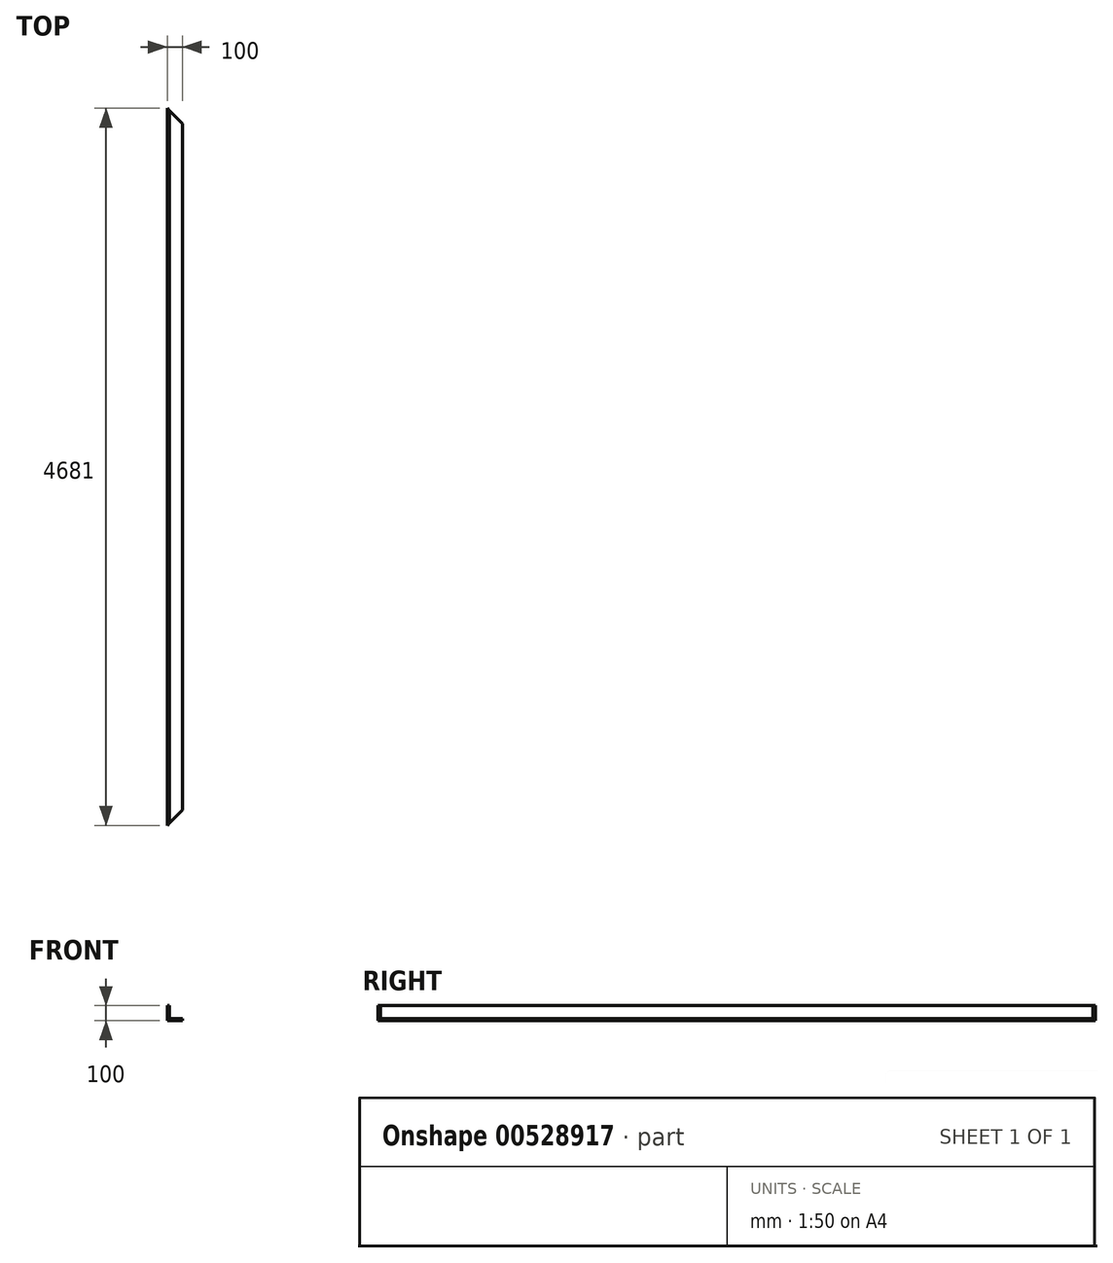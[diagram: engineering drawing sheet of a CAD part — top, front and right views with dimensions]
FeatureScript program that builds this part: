
annotation { "Feature Type Name" : "Feature", "Feature Type Description" : "" }
export const myFeature = defineFeature(function(context is Context, id is Id, definition is map)
    precondition{}
    {
        {
            var Q0;
            Q0=qCreatedBy(makeId("Top.planeOp"),FACE);
            var sketch = newSketch(context, id + "F0", { "sketchPlane" : qUnion([Q0])});
            skLineSegment(sketch, "E0", {"start": v(0, -2340.5) * mm, "end": v(0, 2340.5) * mm});
            skLineSegment(sketch, "E1", {"start": v(-100, -2240.5) * mm, "end": v(-100, 2240.5) * mm});
            skLineSegment(sketch, "E2", {"start": v(0, -2340.5) * mm, "end": v(-100, -2240.5) * mm});
            skLineSegment(sketch, "E3", {"start": v(0, 2340.5) * mm, "end": v(-100, 2240.5) * mm});
            skSolve(sketch);
        }
        {
            var Q0;
            Q0=makeQuery(id+"F0.imprint","IMPRINT",FACE,{"disambiguationData":[TD([[makeQuery(id+"F0.imprint","IMPRINT",EDGE,{"derivedFrom":sQuery(id+"F0.wireOp",EDGE,"E0")}),1.0]])]});
            extrude(context, id + "F1", {"entities" : qUnion([Q0]), "depth" : 15 * mm, "offsetDistance" : 25 * mm});
        }
        {
            var Q0;
            Q0=makeQuery(id+"F1.opExtrude","CAP_FACE",FACE,{"disambiguationData":[OSD([sQuery(id+"F0.wireOp",EDGE,"E0"),sQuery(id+"F0.wireOp",EDGE,"E1"),sQuery(id+"F0.wireOp",EDGE,"E2"),sQuery(id+"F0.wireOp",EDGE,"E3")])],"isStart":false});
            var sketch = newSketch(context, id + "F2", { "sketchPlane" : qUnion([Q0])});
            skLineSegment(sketch, "E4.0", {"start": v(0, -2340.5) * mm, "end": v(0, 2340.5) * mm});
            skLineSegment(sketch, "E5", {"start": v(-15, 2325.5) * mm, "end": v(-15, -2325.5) * mm});
            skLineSegment(sketch, "E6", {"start": v(0, 2340.5) * mm, "end": v(-15, 2325.5) * mm});
            skLineSegment(sketch, "E7", {"start": v(-15, -2325.5) * mm, "end": v(0, -2340.5) * mm});
            skSolve(sketch);
        }
        {
            var Q0;
            Q0=makeQuery(id+"F2.imprint","IMPRINT",FACE,{"disambiguationData":[TD([[makeQuery(id+"F2.imprint","IMPRINT",EDGE,{"derivedFrom":sQuery(id+"F2.wireOp",EDGE,"E4.0")}),1.0]])]});
            extrude(context, id + "F3", {"entities" : qUnion([Q0]), "operationType" : NewBodyOperationType.ADD, "depth" : (100 - 15) * mm, "offsetDistance" : 25 * mm});
        }
        {
            var Q0;
            Q0=makeQuery(id+"F1.opExtrude","SWEPT_BODY",BODY,{"disambiguationData":[OSD([sQuery(id+"F0.wireOp",EDGE,"E0"),sQuery(id+"F0.wireOp",EDGE,"E1"),sQuery(id+"F0.wireOp",EDGE,"E2"),sQuery(id+"F0.wireOp",EDGE,"E3")])]});
            var Q1;
            Q1=makeQuery(id+"F3.boolean.opBoolean","MERGE",FACE,{"derivedFrom":[makeQuery(id+"F1.opExtrude","SWEPT_FACE",FACE,{"disambiguationData":[OSD([sQuery(id+"F0.wireOp",EDGE,"E0")])]}),makeQuery(id+"F3.opExtrude","SWEPT_FACE",FACE,{"disambiguationData":[OSD([sQuery(id+"F2.wireOp",EDGE,"E4.0")])]})]});
            mirror(context, id + "F4", {"entities" : qUnion([Q0]), "mirrorPlane" : qUnion([Q1])});
        }
        {
            var Q0;
            Q0=makeQuery(id+"F1.opExtrude","SWEPT_BODY",BODY,{"disambiguationData":[OSD([sQuery(id+"F0.wireOp",EDGE,"E0"),sQuery(id+"F0.wireOp",EDGE,"E1"),sQuery(id+"F0.wireOp",EDGE,"E2"),sQuery(id+"F0.wireOp",EDGE,"E3")])]});
            deleteBodies(context, id + "F5", {"entities" : qUnion([Q0])});
        }
    });
